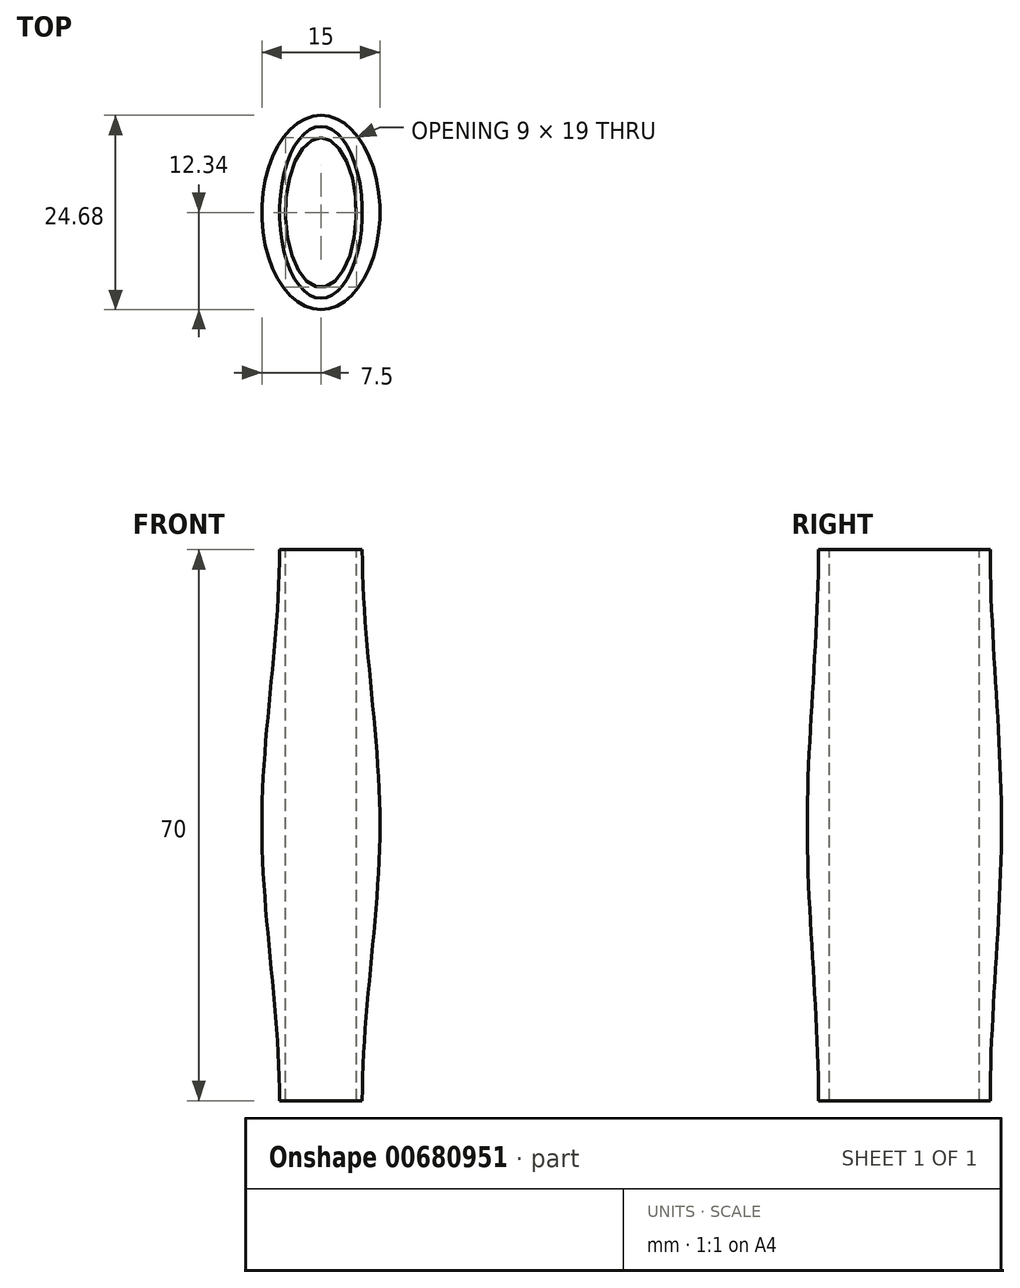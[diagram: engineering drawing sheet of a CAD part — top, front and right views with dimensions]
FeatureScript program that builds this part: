
annotation { "Feature Type Name" : "Feature", "Feature Type Description" : "" }
export const myFeature = defineFeature(function(context is Context, id is Id, definition is map)
    precondition{}
    {
        {
            var Q0;
            Q0=qCreatedBy(makeId("Top.planeOp"),FACE);
            var sketch = newSketch(context, id + "F0", { "sketchPlane" : qUnion([Q0])});
            skEllipticalArc(sketch, "E0", {});
            skLineSegment(sketch, "E1", {"start": v(0, -12.34) * mm, "end": v(0, 12.34) * mm});
            const initialGuessF0  = {"E0": [0, 0, 0, -1, 0.012335, 0.0075, 3.141592653589793, 0]};
            skSetInitialGuess(sketch, initialGuessF0);
            skSolve(sketch);
        }
        {
            var Q0;
            Q0=qCreatedBy(makeId("Top.planeOp"),FACE);
            cPlane(context, id + "F1", {"entities" : qUnion([Q0]), "cplaneType" : CPlaneType.OFFSET, "offset" : 35 * mm, "width" : 150 * mm, "height" : 150 * mm});
        }
        {
            var Q0;
            Q0=qCreatedBy(id+"F1.planeOp",FACE);
            var sketch = newSketch(context, id + "F2", { "sketchPlane" : qUnion([Q0])});
            skEllipticalArc(sketch, "E2", {});
            skLineSegment(sketch, "E3", {"start": v(0, 10.91) * mm, "end": v(0, -10.91) * mm});
            const initialGuessF2  = {"E2": [0, 0, 0, 1, 0.010911500000000001, 0.005249500000000001, 0, 3.141592653589793]};
            skSetInitialGuess(sketch, initialGuessF2);
            skSolve(sketch);
        }
        {
            var Q0;
            Q0=makeQuery(id+"F0.imprint","IMPRINT",FACE,{"disambiguationData":[TD([[makeQuery(id+"F0.imprint","IMPRINT",EDGE,{"derivedFrom":sQuery(id+"F0.wireOp",EDGE,"E0")}),1.0]])]});
            var Q1;
            Q1=makeQuery(id+"F2.imprint","IMPRINT",FACE,{"disambiguationData":[TD([[makeQuery(id+"F2.imprint","IMPRINT",EDGE,{"derivedFrom":sQuery(id+"F2.wireOp",EDGE,"E2")}),1.0]])]});
            loft(context, id + "F3", {"startCondition" : LoftEndDerivativeType.NORMAL_TO_PROFILE, "startMagnitude" : 1, "endCondition" : LoftEndDerivativeType.NORMAL_TO_PROFILE, "endMagnitude" : 1, "sheetProfilesArray" : [{ "sheetProfileEntities" : qUnion([Q0]) }, { "sheetProfileEntities" : qUnion([Q1]) }]});
        }
        {
            var Q0;
            Q0=makeQuery(id+"F3.opLoft","SWEPT_BODY",BODY,{"disambiguationData":[OSD([makeQuery(id+"F0.imprint","IMPRINT",FACE,{"disambiguationData":[TD([[makeQuery(id+"F0.imprint","IMPRINT",EDGE,{"derivedFrom":sQuery(id+"F0.wireOp",EDGE,"E0")}),1.0]])]}),makeQuery(id+"F2.imprint","IMPRINT",FACE,{"disambiguationData":[TD([[makeQuery(id+"F2.imprint","IMPRINT",EDGE,{"derivedFrom":sQuery(id+"F2.wireOp",EDGE,"E2")}),1.0]])]})])]});
            var Q1;
            Q1=qCreatedBy(makeId("Right.planeOp"),FACE);
            mirror(context, id + "F4", {"operationType" : NewBodyOperationType.ADD, "entities" : qUnion([Q0]), "mirrorPlane" : qUnion([Q1])});
        }
        {
            var Q0;
            Q0=makeQuery(id+"F3.opLoft","SWEPT_BODY",BODY,{"disambiguationData":[OSD([makeQuery(id+"F0.imprint","IMPRINT",FACE,{"disambiguationData":[TD([[makeQuery(id+"F0.imprint","IMPRINT",EDGE,{"derivedFrom":sQuery(id+"F0.wireOp",EDGE,"E0")}),1.0]])]}),makeQuery(id+"F2.imprint","IMPRINT",FACE,{"disambiguationData":[TD([[makeQuery(id+"F2.imprint","IMPRINT",EDGE,{"derivedFrom":sQuery(id+"F2.wireOp",EDGE,"E2")}),1.0]])]})])]});
            var Q1;
            Q1=qCreatedBy(makeId("Top.planeOp"),FACE);
            mirror(context, id + "F5", {"operationType" : NewBodyOperationType.ADD, "entities" : qUnion([Q0]), "mirrorPlane" : qUnion([Q1])});
        }
        {
            var Q0;
            {var subQ0=makeQuery(id+"F3.opLoft","CAP_FACE",FACE,{"disambiguationData":[OSD([makeQuery(id+"F2.imprint","IMPRINT",FACE,{"disambiguationData":[TD([[makeQuery(id+"F2.imprint","IMPRINT",EDGE,{"derivedFrom":sQuery(id+"F2.wireOp",EDGE,"E2")}),1.0]])]})])],"isStart":true});Q0=makeQuery(id+"F4.boolean.opBoolean","MERGE",FACE,{"derivedFrom":[subQ0,makeQuery(id+"F4.opPattern","COPY",FACE,{"derivedFrom":subQ0,"instanceName":"1"})]});}
            var sketch = newSketch(context, id + "F6", { "sketchPlane" : qUnion([Q0])});
            skEllipse(sketch, "E4", {"center": v(0, 0) * mm, "majorRadius": 9.5 * mm, "minorRadius": 4.5 * mm, "majorAxis": v(0, 1)});
            skSolve(sketch);
        }
        {
            var Q0;
            Q0=makeQuery(id+"F6.imprint","IMPRINT",FACE,{"disambiguationData":[TD([[makeQuery(id+"F6.imprint","IMPRINT",EDGE,{"derivedFrom":sQuery(id+"F6.wireOp",EDGE,"E4")}),1.0]])]});
            extrude(context, id + "F7", {"entities" : qUnion([Q0]), "operationType" : NewBodyOperationType.REMOVE, "oppositeDirection" : true, "depth" : 70 * mm, "offsetDistance" : 25 * mm});
        }
    });
